# Revit family: Mailboxes_Outdoor_Parcel_Locker-Salsbury_Industries-Type_I_II
name_source: partatom
category: Specialty Equipment
revit_build: Autodesk Revit 2016 (Build: 20150714_1515(x64)
units: mm (PartAtom-declared; Revit-internal decimal feet)

## family parameters
Always vertical = Yes
Cut with Voids When Loaded = No
OmniClass Number = 23.40.90.14.11
OmniClass Title = Mail Boxes
Part Type = Normal
Room Calculation Point = No
Round Connector Dimension = Use Diameter
Shared = No
Work Plane-Based = Yes

## types (2) — shared parameters
Assembly Code = E1010900
Assembly Description = Other Commercial Equipment
Box Height = 48.025 "
Depth = 17.97 "
Door Slot R1 = 3300 Series OPL Parcel Configurations : OPL Parcel Door
Door Slot R2 = 3300 Series OPL Parcel Configurations : OPL Parcel Door
Height = 62.045 "
Lock Material = Stainless Steel - Salsbury Finish -  Polished
Manufacturer = Salsbury Industries
MasterFormat Number = 10 55 26
MasterFormat Title = Postal Specialties
OmniClass 23 Number = 23.40.90.14.11
OmniClass 23 Title = Mail Boxes
Pedestal Height = 14.5 "
Type Comments = Outdoor Parcel Locker (OPL) - Includes Pedestal
URL = www.mailboxes.com
Version = 3.0 (02/28/19)

## per-type parameters (varying)
| type | Center Gap Offset | Description | Door Slot L1 | Door Slot L2 | Visible Dividers | Width |
| 3304 | 12.885 " | 4 Parcel Lockers - Type II - USPS Access | 3300 Series OPL Parcel Configurations : OPL Parcel Door | 3300 Series OPL Parcel Configurations : OPL Parcel Door | Yes | 30.51 " |
| 3302 | 12.879 " | 2 Parcel Lockers - Type I - USPS Access | 3300 Series OPL Parcel Configurations : Empty | 3300 Series OPL Parcel Configurations : Empty | No | 16.155 " |

note: column(s) folded — value = type name in every type: Model

## geometry (parser evidence)
native form markers: Sweep x8
no freeform markers — native parametric forms only
